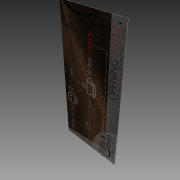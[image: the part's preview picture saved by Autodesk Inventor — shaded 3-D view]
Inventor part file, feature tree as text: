
AUTODESK INVENTOR PART (.ipt)
format: ipt  version: 2015 (Build 190159000, 159)  size: 1,199,616 bytes
history: native  units: mm
features: other x4, sketch x3, extrude x1
ambient origin geometry x8: Origin, YZ Plane, XZ Plane, XY Plane, X Axis, Y Axis, Z Axis, Center Point
bodies: Solid1 (feature_tree)
feature tree (8):
  extrude  "Extrusion1"  Depth=210.0mm
  sketch  "Sketch2"  dims[d2=0.5mm d3=0.0mm]
  other  "Decal1"
  other  "Decal2"
  sketch  "Sketch1"  dims[d0=99.0mm d1=210.0mm]
  other  "Image1"
  sketch  "Sketch3"
  other  "Image3"
